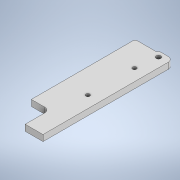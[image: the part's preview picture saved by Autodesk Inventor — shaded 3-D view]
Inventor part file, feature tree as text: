
AUTODESK INVENTOR PART (.ipt)
format: ipt  version: 2021 (Build 250183000, 183)  size: 156,160 bytes
history: native  units: mm
features: sketch x4, extrude x2, hole x2, fillet x1
ambient origin geometry x8: Origin, YZ Plane, XZ Plane, XY Plane, X Axis, Y Axis, Z Axis, Center Point
bodies: Solid1 (feature_tree)
feature tree (9):
  extrude  "Extrusion1"  Depth=104.5mm
  hole  "Hole1"  [1 undecoded]
  extrude  "Extrusion2"  Depth=5.0mm
  hole  "Hole2"  [1 undecoded]
  fillet  "Fillet1"  Radius=15.0mm
  sketch  "Sketch1"  dims[d0=29.5mm d1=104.5mm]
  sketch  "Sketch2"  dims[d7=15.0mm d8=2.0mm]
  sketch  "Sketch3"  dims[d10=5.0mm d11=0.0mm d13=46.0mm]
  sketch  "Sketch4"  dims[d14=84.0mm d15=3.2mm d16=6.0mm d17=4.0mm d18=2.0mm d19=90.0deg d20=8.0mm d21=20.594885mm d23=20.0mm d26=15.0mm d27=20.0mm d28=4.0mm d29=0.0mm d30=0.0mm d31=7.5mm d33=3.8mm d34=6.0mm d35=4.0mm d36=2.0mm d37=90.0deg d38=8.0mm d39=20.594885mm d40=12.0mm d41=1.5mm d42=4.0mm d43=4.5mm d44=2.0mm]
note: 2 required parameter values undecoded (feature->parameter linkage not recoverable at this tier; creation-order binding heuristic only, values carry confidence <= 0.55)
